# Revit family: BE_51143.6_de_DE
name_source: partatom
category: Leuchten
units: mm (PartAtom-declared; Revit-internal decimal feet)

## family parameters
Basisbauteil = Fläche
Beim Laden mit Abzugskörper schneiden = Ja
Bemaßung runder Anschluss = Durchmesser verwenden
Gemeinsam genutzt = Nein
Lichtquelle = Ja
Raumberechnungspunkt = Ja
Teiletyp = Normal

## types (1)
- BEGA_51143.6_K3
    AC/DC = AC/DC
    Aktualisierung = 2023-01-25T04:00:03
    BEGA_Dummy = Nein
    BEGA_IES = Ja
    BEGA_Intern = Ja
    BEGA_Intern_Konstruktion = Ja
    BEGA_Intern_an = Ja
    BEGA_Intern_aus = Ja
    Befestigungsabstand = 90 x 38 mm
    Befestigungsbohrung = Ø 4,5 mm
    Beschreibung = Wandleuchte
    Beschreibung_Sonderanfertigung = Hier können Sie Informationen zur Sonderanfertigung eintragen.
    Bestellnummer = 51143.6K3
    CE_Konformität = ja
    Datei für fotometrisches Netz = BE_51143-6K3.ies
    Energieeffizienzklasse = LED A++ - A
    Farbfilter = 16777215
    Farbtemperatur = 3000 K
    Farbtemperaturverschiebung bei Dämpfen der Lampe = <Keine Auswahl>
    Farbwiedergabeindex = CRI > 80
    Frequenz = 0/50-60 Hz
    Gewicht = 0.93 kg
    Hersteller = BEGA
    LED_Modulbezeichnung = 2x LED-0986/930
    Lampe = LED 17 W
    Lampenlichtstrom = 2400 lm
    Lastklassifizierung = Beleuchtung
    Lebensdauerkriterien = L70B50 @ 25 °C = 175000 h
    Leuchtenlichtstrom = 886 lm
    Logo = <Keine Auswahl>
    M_A = Nein
    M_G = Nein
    M_W = Nein
    Material_08 = BEGA_Oberfläche_Stahl_verzinkt
    Material_14 = BEGA_Kunststoff_opal
    Material_15 = BEGA_Leuchtmedium_matt
    Material_22 = BEGA_Oberfläche_Aluminium_matt
    Material_29 = BEGA_Oberfläche_Kupfer_matt
    Material_34 = BEGA_Oberfläche_Samtweiss_matt
    Modell = 51143.6K3
    Neigungswinkel = 0.00°
    Produktdatenblatt = https://cdn.bega.com
    Scheinlast = 0 VA
    Schutzart = IP 20
    Schutzklasse = I
    Sonderanfertigung = Nein
    Spannung = 240 V
    URL = https://www.bega.com
    Umgebungstemperatur = 25 °C
    Vorgabe-Ansicht = 0 mm  [stored 0 ft]

note: [stored X ft] marks values corroborated as IEEE doubles in the binary element streams (Revit-internal decimal feet)
